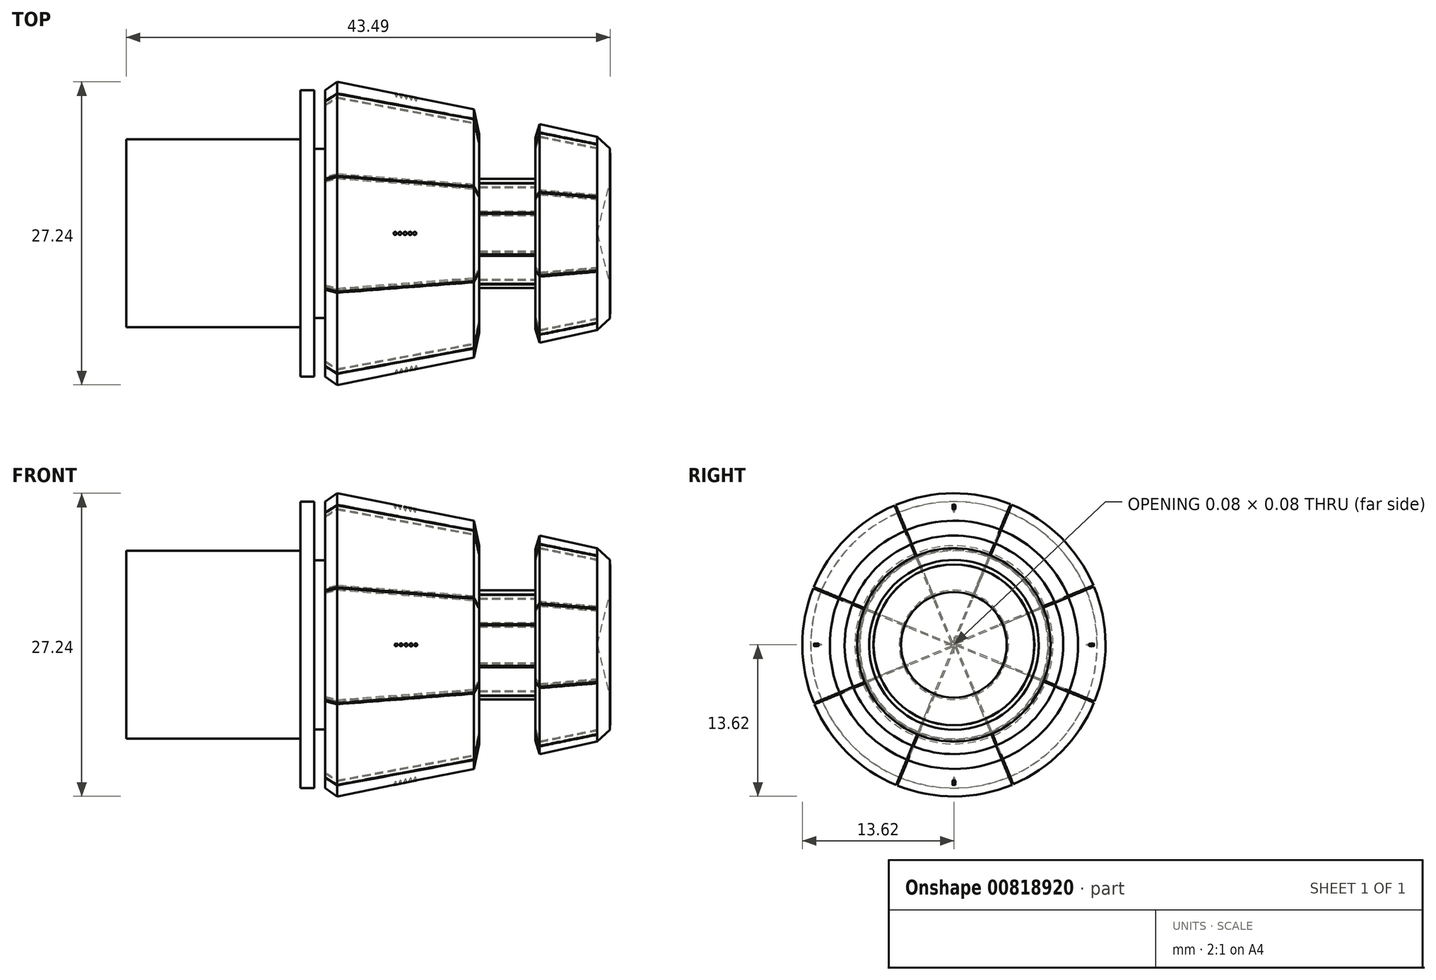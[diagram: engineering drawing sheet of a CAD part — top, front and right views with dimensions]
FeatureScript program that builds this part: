
annotation { "Feature Type Name" : "Feature", "Feature Type Description" : "" }
export const myFeature = defineFeature(function(context is Context, id is Id, definition is map)
    precondition{}
    {
        {
            var Q0;
            Q0=qCreatedBy(makeId("Front.planeOp"),FACE);
            var sketch = newSketch(context, id + "F0", { "sketchPlane" : qUnion([Q0])});
            skLineSegment(sketch, "E0", {"start": v(4.43, 0) * mm, "end": v(4.43, 12.88) * mm});
            skLineSegment(sketch, "E1", {"start": v(4.43, 12.88) * mm, "end": v(5.5, 13.62) * mm});
            skLineSegment(sketch, "E2", {"start": v(5.5, 13.62) * mm, "end": v(5.5, 0) * mm});
            skLineSegment(sketch, "E3", {"start": v(5.5, 0) * mm, "end": v(4.43, 0) * mm});
            skLineSegment(sketch, "E4", {"start": v(5.5, 13.62) * mm, "end": v(17.79, 11.15) * mm});
            skLineSegment(sketch, "E5", {"start": v(17.79, 11.15) * mm, "end": v(17.79, 0) * mm});
            skLineSegment(sketch, "E6", {"start": v(17.79, 0) * mm, "end": v(5.5, 0) * mm});
            skLineSegment(sketch, "E7", {"start": v(17.79, 11.15) * mm, "end": v(18.26, 8.9) * mm});
            skLineSegment(sketch, "E8", {"start": v(18.26, 8.9) * mm, "end": v(18.26, 0) * mm});
            skLineSegment(sketch, "E9", {"start": v(18.26, 0) * mm, "end": v(17.79, 0) * mm});
            skLineSegment(sketch, "E10", {"start": v(23.33, 8.59) * mm, "end": v(23.33, 0) * mm});
            skLineSegment(sketch, "E11", {"start": v(23.33, 0) * mm, "end": v(18.26, 0) * mm});
            skLineSegment(sketch, "E12", {"start": v(4.43, 0) * mm, "end": v(3.45, 0) * mm});
            skLineSegment(sketch, "E13", {"start": v(3.45, 0) * mm, "end": v(3.45, 7.6) * mm});
            skLineSegment(sketch, "E14", {"start": v(3.45, 7.6) * mm, "end": v(4.43, 7.6) * mm});
            skLineSegment(sketch, "E15", {"start": v(4.43, 7.6) * mm, "end": v(4.43, 0) * mm});
            skLineSegment(sketch, "E16", {"start": v(3.45, 0) * mm, "end": v(2.2, 0) * mm});
            skLineSegment(sketch, "E17", {"start": v(2.2, 0) * mm, "end": v(2.2, 12.87) * mm});
            skLineSegment(sketch, "E18", {"start": v(2.2, 12.87) * mm, "end": v(3.45, 12.87) * mm});
            skLineSegment(sketch, "E19", {"start": v(3.45, 12.87) * mm, "end": v(3.45, 7.6) * mm});
            skLineSegment(sketch, "E20", {"start": v(23.33, 8.59) * mm, "end": v(23.72, 9.82) * mm});
            skPoint(sketch, "E21.startSnap0", {"position": v(3.94, 7.6) * mm});
            skLineSegment(sketch, "E22", {"start": v(2.2, 8.45) * mm, "end": v(2.2, 0) * mm});
            skLineSegment(sketch, "E23", {"start": v(-13.45, 8.45) * mm, "end": v(-13.45, 0) * mm});
            skLineSegment(sketch, "E24", {"start": v(-13.45, 8.45) * mm, "end": v(2.2, 8.45) * mm});
            skLineSegment(sketch, "E25", {"start": v(-13.45, 0) * mm, "end": v(2.2, 0) * mm});
            skPoint(sketch, "E26", {"position": v(28.88, 8.7) * mm});
            skLineSegment(sketch, "E27", {"start": v(28.88, 8.7) * mm, "end": v(28.88, 0) * mm});
            skLineSegment(sketch, "E28", {"start": v(30.03, 7.63) * mm, "end": v(28.88, 8.7) * mm});
            skLineSegment(sketch, "E29", {"start": v(23.72, 9.82) * mm, "end": v(28.88, 8.7) * mm});
            skLineSegment(sketch, "E30", {"start": v(23.72, 9.82) * mm, "end": v(23.72, 0) * mm});
            skLineSegment(sketch, "E31", {"start": v(23.72, 0) * mm, "end": v(23.33, 0) * mm});
            skLineSegment(sketch, "E32", {"start": v(18.26, 0) * mm, "end": v(23.33, 0) * mm});
            skLineSegment(sketch, "E33", {"start": v(23.33, 4.91) * mm, "end": v(18.26, 4.91) * mm});
            skLineSegment(sketch, "E34", {"start": v(18.26, 4.91) * mm, "end": v(18.26, 0) * mm});
            skLineSegment(sketch, "E35", {"start": v(28.88, 0) * mm, "end": v(28.88, 8.7) * mm});
            skLineSegment(sketch, "E36", {"start": v(30.03, 7.63) * mm, "end": v(30.03, 4.75) * mm});
            skLineSegment(sketch, "E37", {"start": v(30.03, 4.75) * mm, "end": v(28.88, 0) * mm});
            skLineSegment(sketch, "E38", {"start": v(23.72, 0) * mm, "end": v(28.88, 0) * mm});
            skSolve(sketch);
        }
        {
            var Q0;
            Q0=qSketchRegion(id+"F0",true);
            var Q1;
            Q1=sQuery(id+"F0.wireOp",EDGE,"E12");
            revolve(context, id + "F1", {"surfaceOperationType" : NewSurfaceOperationType.NEW, "entities" : qUnion([Q0]), "axis" : qUnion([Q1]), "revolveType" : RevolveType.FULL});
        }
        {
            var Q0;
            Q0=qCreatedBy(makeId("Right.planeOp"),FACE);
            var sketch = newSketch(context, id + "F2", { "sketchPlane" : qUnion([Q0])});
            skLineSegment(sketch, "E39.bottom", {"start": v(-0.13, 0.07) * mm, "end": v(0, 0.02) * mm});
            skLineSegment(sketch, "E39.top", {"start": v(7.3, 17.98) * mm, "end": v(7.41, 17.93) * mm});
            skLineSegment(sketch, "E39.left", {"start": v(0, 0.02) * mm, "end": v(7.41, 17.93) * mm});
            skLineSegment(sketch, "E39.right", {"start": v(-0.13, 0.07) * mm, "end": v(7.3, 17.98) * mm});
            skLineSegment(sketch, "E40.1.0", {"start": v(-0.14, -0.04) * mm, "end": v(-7.56, 17.87) * mm});
            skLineSegment(sketch, "E40.1.1", {"start": v(-0.02, 0) * mm, "end": v(-7.44, 17.92) * mm});
            skLineSegment(sketch, "E40.1.2", {"start": v(-0.14, -0.04) * mm, "end": v(-0.02, 0) * mm});
            skLineSegment(sketch, "E40.1.3", {"start": v(-7.56, 17.87) * mm, "end": v(-7.44, 17.92) * mm});
            skLineSegment(sketch, "E40.2.0", {"start": v(-0.07, -0.13) * mm, "end": v(-17.98, 7.3) * mm});
            skLineSegment(sketch, "E40.2.1", {"start": v(-0.02, 0) * mm, "end": v(-17.93, 7.41) * mm});
            skLineSegment(sketch, "E40.2.2", {"start": v(-0.07, -0.13) * mm, "end": v(-0.02, 0) * mm});
            skLineSegment(sketch, "E40.2.3", {"start": v(-17.98, 7.3) * mm, "end": v(-17.93, 7.41) * mm});
            skLineSegment(sketch, "E40.3.0", {"start": v(0.04, -0.14) * mm, "end": v(-17.87, -7.56) * mm});
            skLineSegment(sketch, "E40.3.1", {"start": v(0, -0.02) * mm, "end": v(-17.92, -7.44) * mm});
            skLineSegment(sketch, "E40.3.2", {"start": v(0.04, -0.14) * mm, "end": v(0, -0.02) * mm});
            skLineSegment(sketch, "E40.3.3", {"start": v(-17.87, -7.56) * mm, "end": v(-17.92, -7.44) * mm});
            skLineSegment(sketch, "E40.4.0", {"start": v(0.13, -0.07) * mm, "end": v(-7.3, -17.98) * mm});
            skLineSegment(sketch, "E40.4.1", {"start": v(0, -0.02) * mm, "end": v(-7.41, -17.93) * mm});
            skLineSegment(sketch, "E40.4.2", {"start": v(0.13, -0.07) * mm, "end": v(0, -0.02) * mm});
            skLineSegment(sketch, "E40.4.3", {"start": v(-7.3, -17.98) * mm, "end": v(-7.41, -17.93) * mm});
            skLineSegment(sketch, "E40.5.0", {"start": v(0.14, 0.04) * mm, "end": v(7.56, -17.87) * mm});
            skLineSegment(sketch, "E40.5.1", {"start": v(0.02, 0) * mm, "end": v(7.44, -17.92) * mm});
            skLineSegment(sketch, "E40.5.2", {"start": v(0.14, 0.04) * mm, "end": v(0.02, 0) * mm});
            skLineSegment(sketch, "E40.5.3", {"start": v(7.56, -17.87) * mm, "end": v(7.44, -17.92) * mm});
            skLineSegment(sketch, "E40.6.0", {"start": v(0.07, 0.13) * mm, "end": v(17.98, -7.3) * mm});
            skLineSegment(sketch, "E40.6.1", {"start": v(0.02, 0) * mm, "end": v(17.93, -7.41) * mm});
            skLineSegment(sketch, "E40.6.2", {"start": v(0.07, 0.13) * mm, "end": v(0.02, 0) * mm});
            skLineSegment(sketch, "E40.6.3", {"start": v(17.98, -7.3) * mm, "end": v(17.93, -7.41) * mm});
            skLineSegment(sketch, "E40.7.0", {"start": v(-0.04, 0.14) * mm, "end": v(17.87, 7.56) * mm});
            skLineSegment(sketch, "E40.7.1", {"start": v(0, 0.02) * mm, "end": v(17.92, 7.44) * mm});
            skLineSegment(sketch, "E40.7.2", {"start": v(-0.04, 0.14) * mm, "end": v(0, 0.02) * mm});
            skLineSegment(sketch, "E40.7.3", {"start": v(17.87, 7.56) * mm, "end": v(17.92, 7.44) * mm});
            skPoint(sketch, "E40.center", {"position": v(0, 0) * mm});
            skSolve(sketch);
        }
        {
            var Q0;
            Q0 = qSketchRegion(id + "F2", true);
            var Q1;
            Q1=makeQuery(id+"F1.opRevolve","SWEPT_VERTEX",VERTEX,{"disambiguationData":[OSD([sQuery(id+"F0.wireOp",EDGE,"E35"),sQuery(id+"F0.wireOp",EDGE,"E37"),sQuery(id+"F0.wireOp",EDGE,"E38")])]});
            var Q2;
            Q2=makeQuery(id+"F1.opRevolve","SWEPT_FACE",FACE,{"disambiguationData":[OSD([sQuery(id+"F0.wireOp",EDGE,"E0")])]});
            extrude(context, id + "F3", {"entities" : qUnion([Q0]), "operationType" : NewBodyOperationType.REMOVE, "endBound" : BoundingType.UP_TO_VERTEX, "depth" : 37.08 * mm, "endBoundEntityVertex" : qUnion([Q1]), "offsetDistance" : 25.4 * mm, "hasSecondDirection" : true, "secondDirectionBound" : SecondDirectionBoundingType.UP_TO_SURFACE, "secondDirectionOppositeDirection" : false, "secondDirectionDepth" : 4.32 * mm, "secondDirectionBoundEntityFace" : qUnion([Q2])});
        }
        {
            var Q0;
            Q0=qCreatedBy(makeId("Front.planeOp"),FACE);
            var sketch = newSketch(context, id + "F4", { "sketchPlane" : qUnion([Q0])});
            skLineSegment(sketch, "E41", {"start": v(4.44, 0) * mm, "end": v(4.44, 12.88) * mm});
            skLineSegment(sketch, "E42", {"start": v(4.44, 12.48) * mm, "end": v(5.52, 13.22) * mm});
            skLineSegment(sketch, "E43", {"start": v(5.52, 13.62) * mm, "end": v(5.52, 0) * mm});
            skLineSegment(sketch, "E44", {"start": v(5.52, 0) * mm, "end": v(4.44, 0) * mm});
            skLineSegment(sketch, "E45", {"start": v(5.52, 13.22) * mm, "end": v(17.8, 10.75) * mm});
            skLineSegment(sketch, "E46", {"start": v(17.8, 11.15) * mm, "end": v(17.8, 0) * mm});
            skLineSegment(sketch, "E47", {"start": v(17.8, 0) * mm, "end": v(5.52, 0) * mm});
            skLineSegment(sketch, "E48", {"start": v(17.8, 10.75) * mm, "end": v(18.27, 8.5) * mm});
            skLineSegment(sketch, "E49", {"start": v(18.27, 8.9) * mm, "end": v(18.27, 0) * mm});
            skLineSegment(sketch, "E50", {"start": v(18.27, 0) * mm, "end": v(17.8, 0) * mm});
            skLineSegment(sketch, "E51", {"start": v(23.34, 8.59) * mm, "end": v(23.34, 0) * mm});
            skLineSegment(sketch, "E52", {"start": v(23.34, 0) * mm, "end": v(18.27, 0) * mm});
            skLineSegment(sketch, "E53", {"start": v(4.44, 7.6) * mm, "end": v(4.44, 0) * mm});
            skLineSegment(sketch, "E54", {"start": v(23.34, 8.18) * mm, "end": v(23.72, 9.42) * mm});
            skLineSegment(sketch, "E55", {"start": v(2.2, 8.45) * mm, "end": v(2.2, 0) * mm});
            skPoint(sketch, "E56", {"position": v(28.89, 8.29) * mm});
            skLineSegment(sketch, "E57", {"start": v(28.89, 8.7) * mm, "end": v(28.89, 0) * mm});
            skLineSegment(sketch, "E58", {"start": v(30.04, 7.22) * mm, "end": v(28.89, 8.29) * mm});
            skLineSegment(sketch, "E59", {"start": v(23.72, 9.42) * mm, "end": v(28.89, 8.29) * mm});
            skLineSegment(sketch, "E60", {"start": v(23.72, 9.82) * mm, "end": v(23.72, 0) * mm});
            skLineSegment(sketch, "E61", {"start": v(23.72, 0) * mm, "end": v(23.34, 0) * mm});
            skLineSegment(sketch, "E62", {"start": v(18.27, 0) * mm, "end": v(23.34, 0) * mm});
            skLineSegment(sketch, "E63", {"start": v(23.34, 4.5) * mm, "end": v(18.27, 4.5) * mm});
            skLineSegment(sketch, "E64", {"start": v(18.27, 4.91) * mm, "end": v(18.27, 0) * mm});
            skLineSegment(sketch, "E65", {"start": v(28.89, 0) * mm, "end": v(28.89, 8.7) * mm});
            skLineSegment(sketch, "E66", {"start": v(30.04, 7.63) * mm, "end": v(30.04, 4.75) * mm});
            skLineSegment(sketch, "E67", {"start": v(30.04, 4.75) * mm, "end": v(28.89, 0) * mm});
            skLineSegment(sketch, "E68", {"start": v(23.72, 0) * mm, "end": v(28.89, 0) * mm});
            skSolve(sketch);
        }
        {
            var Q0;
            Q0 = qSketchRegion(id + "F4", true);
            var Q1;
            Q1=sQuery(id+"F4.wireOp",EDGE,"E47");
            revolve(context, id + "F5", {"operationType" : NewBodyOperationType.ADD, "surfaceOperationType" : NewSurfaceOperationType.NEW, "entities" : qUnion([Q0]), "axis" : qUnion([Q1]), "revolveType" : RevolveType.FULL});
        }
        {
            var Q0;
            Q0=qCreatedBy(makeId("Top.planeOp"),FACE);
            var sketch = newSketch(context, id + "F6", { "sketchPlane" : qUnion([Q0])});
            skLineSegment(sketch, "E69.MirrorCS", {"start": v(11.9, -12.5) * mm, "end": v(11.74, -12.03) * mm});
            skLineSegment(sketch, "E70.MirrorCS", {"start": v(11.71, -12.5) * mm, "end": v(11.9, -12.5) * mm});
            skLineSegment(sketch, "E71.MirrorCS", {"start": v(11.74, -12.03) * mm, "end": v(11.71, -12.5) * mm});
            skLineSegment(sketch, "E72.MirrorCS", {"start": v(12.35, -12.42) * mm, "end": v(12.2, -11.94) * mm});
            skLineSegment(sketch, "E73.MirrorCS", {"start": v(12.16, -12.4) * mm, "end": v(12.35, -12.42) * mm});
            skLineSegment(sketch, "E74.MirrorCS", {"start": v(12.2, -11.94) * mm, "end": v(12.16, -12.4) * mm});
            skLineSegment(sketch, "E75.MirrorCS", {"start": v(11.44, -12.62) * mm, "end": v(11.28, -12.14) * mm});
            skLineSegment(sketch, "E76.MirrorCS", {"start": v(11.25, -12.6) * mm, "end": v(11.44, -12.62) * mm});
            skLineSegment(sketch, "E77.MirrorCS", {"start": v(11.28, -12.14) * mm, "end": v(11.25, -12.6) * mm});
            skLineSegment(sketch, "E78.MirrorCS", {"start": v(11, -12.71) * mm, "end": v(10.85, -12.24) * mm});
            skLineSegment(sketch, "E79.MirrorCS", {"start": v(10.81, -12.7) * mm, "end": v(11, -12.71) * mm});
            skLineSegment(sketch, "E80.MirrorCS", {"start": v(10.85, -12.24) * mm, "end": v(10.81, -12.7) * mm});
            skLineSegment(sketch, "E81.MirrorCS", {"start": v(12.76, -12.35) * mm, "end": v(12.61, -11.88) * mm});
            skLineSegment(sketch, "E82.MirrorCS", {"start": v(12.58, -12.34) * mm, "end": v(12.76, -12.35) * mm});
            skLineSegment(sketch, "E83.MirrorCS", {"start": v(12.61, -11.88) * mm, "end": v(12.58, -12.34) * mm});
            skLineSegment(sketch, "E84.MirrorCS", {"start": v(11.28, 12.14) * mm, "end": v(11.25, 12.6) * mm});
            skLineSegment(sketch, "E85.MirrorCS", {"start": v(11.71, 12.5) * mm, "end": v(11.9, 12.5) * mm});
            skLineSegment(sketch, "E86.MirrorCS", {"start": v(11.25, 12.6) * mm, "end": v(11.44, 12.62) * mm});
            skLineSegment(sketch, "E87.MirrorCS", {"start": v(12.35, 12.42) * mm, "end": v(12.2, 11.94) * mm});
            skLineSegment(sketch, "E88.MirrorCS", {"start": v(11, 12.71) * mm, "end": v(10.85, 12.24) * mm});
            skLineSegment(sketch, "E89.MirrorCS", {"start": v(10.81, 12.7) * mm, "end": v(11, 12.71) * mm});
            skLineSegment(sketch, "E90.MirrorCS", {"start": v(11.74, 12.03) * mm, "end": v(11.71, 12.5) * mm});
            skLineSegment(sketch, "E91.MirrorCS", {"start": v(12.58, 12.34) * mm, "end": v(12.76, 12.35) * mm});
            skLineSegment(sketch, "E92.MirrorCS", {"start": v(11.44, 12.62) * mm, "end": v(11.28, 12.14) * mm});
            skLineSegment(sketch, "E93.MirrorCS", {"start": v(12.76, 12.35) * mm, "end": v(12.61, 11.88) * mm});
            skLineSegment(sketch, "E94.MirrorCS", {"start": v(10.85, 12.24) * mm, "end": v(10.81, 12.7) * mm});
            skLineSegment(sketch, "E95.MirrorCS", {"start": v(12.61, 11.88) * mm, "end": v(12.58, 12.34) * mm});
            skLineSegment(sketch, "E96.MirrorCS", {"start": v(12.16, 12.4) * mm, "end": v(12.35, 12.42) * mm});
            skLineSegment(sketch, "E97.MirrorCS", {"start": v(11.9, 12.5) * mm, "end": v(11.74, 12.03) * mm});
            skLineSegment(sketch, "E98.MirrorCS", {"start": v(12.2, 11.94) * mm, "end": v(12.16, 12.4) * mm});
            skSolve(sketch);
        }
        {
            var Q0;
            Q0=makeQuery(id+"F6.imprint","IMPRINT",FACE,{"disambiguationData":[TD([[makeQuery(id+"F6.imprint","IMPRINT",EDGE,{"derivedFrom":sQuery(id+"F6.wireOp",EDGE,"E78.MirrorCS")}),1.0]])]});
            var Q1;
            Q1=sQuery(id+"F6.wireOp",EDGE,"E80.MirrorCS");
            revolve(context, id + "F7", {"operationType" : NewBodyOperationType.REMOVE, "surfaceOperationType" : NewSurfaceOperationType.NEW, "entities" : qUnion([Q0]), "axis" : qUnion([Q1]), "revolveType" : RevolveType.FULL, "oppositeDirection" : true});
        }
        {
            var Q0;
            Q0=makeQuery(id+"F6.imprint","IMPRINT",FACE,{"disambiguationData":[TD([[makeQuery(id+"F6.imprint","IMPRINT",EDGE,{"derivedFrom":sQuery(id+"F6.wireOp",EDGE,"E75.MirrorCS")}),1.0]])]});
            var Q1;
            Q1=sQuery(id+"F6.wireOp",EDGE,"E77.MirrorCS");
            revolve(context, id + "F8", {"operationType" : NewBodyOperationType.REMOVE, "surfaceOperationType" : NewSurfaceOperationType.NEW, "entities" : qUnion([Q0]), "axis" : qUnion([Q1]), "revolveType" : RevolveType.FULL, "oppositeDirection" : true});
        }
        {
            var Q0;
            Q0=makeQuery(id+"F6.imprint","IMPRINT",FACE,{"disambiguationData":[TD([[makeQuery(id+"F6.imprint","IMPRINT",EDGE,{"derivedFrom":sQuery(id+"F6.wireOp",EDGE,"E69.MirrorCS")}),1.0]])]});
            var Q1;
            Q1=sQuery(id+"F6.wireOp",EDGE,"E71.MirrorCS");
            revolve(context, id + "F9", {"operationType" : NewBodyOperationType.REMOVE, "surfaceOperationType" : NewSurfaceOperationType.NEW, "entities" : qUnion([Q0]), "axis" : qUnion([Q1]), "revolveType" : RevolveType.FULL, "oppositeDirection" : true});
        }
        {
            var Q0;
            Q0=makeQuery(id+"F6.imprint","IMPRINT",FACE,{"disambiguationData":[TD([[makeQuery(id+"F6.imprint","IMPRINT",EDGE,{"derivedFrom":sQuery(id+"F6.wireOp",EDGE,"E72.MirrorCS")}),1.0]])]});
            var Q1;
            Q1=sQuery(id+"F6.wireOp",EDGE,"E74.MirrorCS");
            revolve(context, id + "F10", {"operationType" : NewBodyOperationType.REMOVE, "surfaceOperationType" : NewSurfaceOperationType.NEW, "entities" : qUnion([Q0]), "axis" : qUnion([Q1]), "revolveType" : RevolveType.FULL, "oppositeDirection" : true});
        }
        {
            var Q0;
            Q0=makeQuery(id+"F6.imprint","IMPRINT",FACE,{"disambiguationData":[TD([[makeQuery(id+"F6.imprint","IMPRINT",EDGE,{"derivedFrom":sQuery(id+"F6.wireOp",EDGE,"E81.MirrorCS")}),1.0]])]});
            var Q1;
            Q1=sQuery(id+"F6.wireOp",EDGE,"E83.MirrorCS");
            revolve(context, id + "F11", {"operationType" : NewBodyOperationType.REMOVE, "surfaceOperationType" : NewSurfaceOperationType.NEW, "entities" : qUnion([Q0]), "axis" : qUnion([Q1]), "revolveType" : RevolveType.FULL, "oppositeDirection" : true});
        }
        {
            var Q0;
            Q0=makeQuery(id+"F6.imprint","IMPRINT",FACE,{"disambiguationData":[TD([[makeQuery(id+"F6.imprint","IMPRINT",EDGE,{"derivedFrom":sQuery(id+"F6.wireOp",EDGE,"E88.MirrorCS")}),-1.0]])]});
            var Q1;
            Q1=sQuery(id+"F6.wireOp",EDGE,"E94.MirrorCS");
            revolve(context, id + "F12", {"operationType" : NewBodyOperationType.REMOVE, "surfaceOperationType" : NewSurfaceOperationType.NEW, "entities" : qUnion([Q0]), "axis" : qUnion([Q1]), "revolveType" : RevolveType.FULL, "oppositeDirection" : true});
        }
        {
            var Q0;
            Q0=makeQuery(id+"F6.imprint","IMPRINT",FACE,{"disambiguationData":[TD([[makeQuery(id+"F6.imprint","IMPRINT",EDGE,{"derivedFrom":sQuery(id+"F6.wireOp",EDGE,"E84.MirrorCS")}),-1.0]])]});
            var Q1;
            Q1=sQuery(id+"F6.wireOp",EDGE,"E84.MirrorCS");
            revolve(context, id + "F13", {"operationType" : NewBodyOperationType.REMOVE, "surfaceOperationType" : NewSurfaceOperationType.NEW, "entities" : qUnion([Q0]), "axis" : qUnion([Q1]), "revolveType" : RevolveType.FULL, "oppositeDirection" : true});
        }
        {
            var Q0;
            Q0=makeQuery(id+"F6.imprint","IMPRINT",FACE,{"disambiguationData":[TD([[makeQuery(id+"F6.imprint","IMPRINT",EDGE,{"derivedFrom":sQuery(id+"F6.wireOp",EDGE,"E85.MirrorCS")}),-1.0]])]});
            var Q1;
            Q1=sQuery(id+"F6.wireOp",EDGE,"E90.MirrorCS");
            revolve(context, id + "F14", {"operationType" : NewBodyOperationType.REMOVE, "surfaceOperationType" : NewSurfaceOperationType.NEW, "entities" : qUnion([Q0]), "axis" : qUnion([Q1]), "revolveType" : RevolveType.FULL, "oppositeDirection" : true});
        }
        {
            var Q0;
            Q0=makeQuery(id+"F6.imprint","IMPRINT",FACE,{"disambiguationData":[TD([[makeQuery(id+"F6.imprint","IMPRINT",EDGE,{"derivedFrom":sQuery(id+"F6.wireOp",EDGE,"E87.MirrorCS")}),-1.0]])]});
            var Q1;
            Q1=sQuery(id+"F6.wireOp",EDGE,"E98.MirrorCS");
            revolve(context, id + "F15", {"operationType" : NewBodyOperationType.REMOVE, "surfaceOperationType" : NewSurfaceOperationType.NEW, "entities" : qUnion([Q0]), "axis" : qUnion([Q1]), "revolveType" : RevolveType.FULL, "oppositeDirection" : true});
        }
        {
            var Q0;
            Q0=makeQuery(id+"F6.imprint","IMPRINT",FACE,{"disambiguationData":[TD([[makeQuery(id+"F6.imprint","IMPRINT",EDGE,{"derivedFrom":sQuery(id+"F6.wireOp",EDGE,"E91.MirrorCS")}),-1.0]])]});
            var Q1;
            Q1=sQuery(id+"F6.wireOp",EDGE,"E95.MirrorCS");
            revolve(context, id + "F16", {"operationType" : NewBodyOperationType.REMOVE, "surfaceOperationType" : NewSurfaceOperationType.NEW, "entities" : qUnion([Q0]), "axis" : qUnion([Q1]), "revolveType" : RevolveType.FULL, "oppositeDirection" : true});
        }
        {
            var Q0;
            Q0=qCreatedBy(makeId("Front.planeOp"),FACE);
            var sketch = newSketch(context, id + "F17", { "sketchPlane" : qUnion([Q0])});
            skLineSegment(sketch, "E99.MirrorCS", {"start": v(11.8, -12.5) * mm, "end": v(11.65, -12.03) * mm});
            skLineSegment(sketch, "E100.MirrorCS", {"start": v(11.62, -12.5) * mm, "end": v(11.8, -12.5) * mm});
            skLineSegment(sketch, "E101.MirrorCS", {"start": v(11.65, -12.03) * mm, "end": v(11.62, -12.5) * mm});
            skLineSegment(sketch, "E102.MirrorCS", {"start": v(12.25, -12.42) * mm, "end": v(12.1, -11.94) * mm});
            skLineSegment(sketch, "E103.MirrorCS", {"start": v(12.07, -12.4) * mm, "end": v(12.25, -12.42) * mm});
            skLineSegment(sketch, "E104.MirrorCS", {"start": v(12.1, -11.94) * mm, "end": v(12.07, -12.4) * mm});
            skLineSegment(sketch, "E105.MirrorCS", {"start": v(11.34, -12.62) * mm, "end": v(11.2, -12.14) * mm});
            skLineSegment(sketch, "E106.MirrorCS", {"start": v(11.16, -12.6) * mm, "end": v(11.34, -12.62) * mm});
            skLineSegment(sketch, "E107.MirrorCS", {"start": v(11.2, -12.14) * mm, "end": v(11.16, -12.6) * mm});
            skLineSegment(sketch, "E108.MirrorCS", {"start": v(10.9, -12.71) * mm, "end": v(10.75, -12.24) * mm});
            skLineSegment(sketch, "E109.MirrorCS", {"start": v(10.72, -12.7) * mm, "end": v(10.9, -12.71) * mm});
            skLineSegment(sketch, "E110.MirrorCS", {"start": v(10.75, -12.24) * mm, "end": v(10.72, -12.7) * mm});
            skLineSegment(sketch, "E111.MirrorCS", {"start": v(12.67, -12.35) * mm, "end": v(12.52, -11.88) * mm});
            skLineSegment(sketch, "E112.MirrorCS", {"start": v(12.49, -12.34) * mm, "end": v(12.67, -12.35) * mm});
            skLineSegment(sketch, "E113.MirrorCS", {"start": v(12.52, -11.88) * mm, "end": v(12.49, -12.34) * mm});
            skLineSegment(sketch, "E114.MirrorCS", {"start": v(11.2, 12.14) * mm, "end": v(11.16, 12.6) * mm});
            skLineSegment(sketch, "E115.MirrorCS", {"start": v(11.62, 12.5) * mm, "end": v(11.8, 12.5) * mm});
            skLineSegment(sketch, "E116.MirrorCS", {"start": v(11.16, 12.6) * mm, "end": v(11.34, 12.62) * mm});
            skLineSegment(sketch, "E117.MirrorCS", {"start": v(12.25, 12.42) * mm, "end": v(12.1, 11.94) * mm});
            skLineSegment(sketch, "E118.MirrorCS", {"start": v(10.9, 12.71) * mm, "end": v(10.75, 12.24) * mm});
            skLineSegment(sketch, "E119.MirrorCS", {"start": v(10.72, 12.7) * mm, "end": v(10.9, 12.71) * mm});
            skLineSegment(sketch, "E120.MirrorCS", {"start": v(11.65, 12.03) * mm, "end": v(11.62, 12.5) * mm});
            skLineSegment(sketch, "E121.MirrorCS", {"start": v(12.49, 12.34) * mm, "end": v(12.67, 12.35) * mm});
            skLineSegment(sketch, "E122.MirrorCS", {"start": v(11.34, 12.62) * mm, "end": v(11.2, 12.14) * mm});
            skLineSegment(sketch, "E123.MirrorCS", {"start": v(12.67, 12.35) * mm, "end": v(12.52, 11.88) * mm});
            skLineSegment(sketch, "E124.MirrorCS", {"start": v(10.75, 12.24) * mm, "end": v(10.72, 12.7) * mm});
            skLineSegment(sketch, "E125.MirrorCS", {"start": v(12.52, 11.88) * mm, "end": v(12.49, 12.34) * mm});
            skLineSegment(sketch, "E126.MirrorCS", {"start": v(12.07, 12.4) * mm, "end": v(12.25, 12.42) * mm});
            skLineSegment(sketch, "E127.MirrorCS", {"start": v(11.8, 12.5) * mm, "end": v(11.65, 12.03) * mm});
            skLineSegment(sketch, "E128.MirrorCS", {"start": v(12.1, 11.94) * mm, "end": v(12.07, 12.4) * mm});
            skSolve(sketch);
        }
        {
            var Q0;
            Q0=makeQuery(id+"F17.imprint","IMPRINT",FACE,{"disambiguationData":[TD([[makeQuery(id+"F17.imprint","IMPRINT",EDGE,{"derivedFrom":sQuery(id+"F17.wireOp",EDGE,"E99.MirrorCS")}),1.0]])]});
            var Q1;
            Q1=sQuery(id+"F17.wireOp",EDGE,"E101.MirrorCS");
            revolve(context, id + "F18", {"operationType" : NewBodyOperationType.REMOVE, "surfaceOperationType" : NewSurfaceOperationType.NEW, "entities" : qUnion([Q0]), "axis" : qUnion([Q1]), "revolveType" : RevolveType.FULL, "oppositeDirection" : true});
        }
        {
            var Q0;
            Q0=makeQuery(id+"F17.imprint","IMPRINT",FACE,{"disambiguationData":[TD([[makeQuery(id+"F17.imprint","IMPRINT",EDGE,{"derivedFrom":sQuery(id+"F17.wireOp",EDGE,"E108.MirrorCS")}),1.0]])]});
            var Q1;
            Q1=sQuery(id+"F17.wireOp",EDGE,"E110.MirrorCS");
            revolve(context, id + "F19", {"operationType" : NewBodyOperationType.REMOVE, "surfaceOperationType" : NewSurfaceOperationType.NEW, "entities" : qUnion([Q0]), "axis" : qUnion([Q1]), "revolveType" : RevolveType.FULL, "oppositeDirection" : true});
        }
        {
            var Q0;
            Q0=makeQuery(id+"F17.imprint","IMPRINT",FACE,{"disambiguationData":[TD([[makeQuery(id+"F17.imprint","IMPRINT",EDGE,{"derivedFrom":sQuery(id+"F17.wireOp",EDGE,"E105.MirrorCS")}),1.0]])]});
            var Q1;
            Q1=sQuery(id+"F17.wireOp",EDGE,"E107.MirrorCS");
            revolve(context, id + "F20", {"operationType" : NewBodyOperationType.REMOVE, "surfaceOperationType" : NewSurfaceOperationType.NEW, "entities" : qUnion([Q0]), "axis" : qUnion([Q1]), "revolveType" : RevolveType.FULL});
        }
        {
            var Q0;
            Q0=makeQuery(id+"F17.imprint","IMPRINT",FACE,{"disambiguationData":[TD([[makeQuery(id+"F17.imprint","IMPRINT",EDGE,{"derivedFrom":sQuery(id+"F17.wireOp",EDGE,"E102.MirrorCS")}),1.0]])]});
            var Q1;
            Q1=sQuery(id+"F17.wireOp",EDGE,"E104.MirrorCS");
            revolve(context, id + "F21", {"operationType" : NewBodyOperationType.REMOVE, "surfaceOperationType" : NewSurfaceOperationType.NEW, "entities" : qUnion([Q0]), "axis" : qUnion([Q1]), "revolveType" : RevolveType.FULL, "oppositeDirection" : true});
        }
        {
            var Q0;
            Q0=makeQuery(id+"F17.imprint","IMPRINT",FACE,{"disambiguationData":[TD([[makeQuery(id+"F17.imprint","IMPRINT",EDGE,{"derivedFrom":sQuery(id+"F17.wireOp",EDGE,"E111.MirrorCS")}),1.0]])]});
            var Q1;
            Q1=sQuery(id+"F17.wireOp",EDGE,"E113.MirrorCS");
            revolve(context, id + "F22", {"operationType" : NewBodyOperationType.REMOVE, "surfaceOperationType" : NewSurfaceOperationType.NEW, "entities" : qUnion([Q0]), "axis" : qUnion([Q1]), "revolveType" : RevolveType.FULL, "oppositeDirection" : true});
        }
        {
            var Q0;
            Q0=makeQuery(id+"F17.imprint","IMPRINT",FACE,{"disambiguationData":[TD([[makeQuery(id+"F17.imprint","IMPRINT",EDGE,{"derivedFrom":sQuery(id+"F17.wireOp",EDGE,"E118.MirrorCS")}),-1.0]])]});
            var Q1;
            Q1=sQuery(id+"F17.wireOp",EDGE,"E124.MirrorCS");
            revolve(context, id + "F23", {"operationType" : NewBodyOperationType.REMOVE, "surfaceOperationType" : NewSurfaceOperationType.NEW, "entities" : qUnion([Q0]), "axis" : qUnion([Q1]), "revolveType" : RevolveType.FULL, "oppositeDirection" : true});
        }
        {
            var Q0;
            Q0=makeQuery(id+"F17.imprint","IMPRINT",FACE,{"disambiguationData":[TD([[makeQuery(id+"F17.imprint","IMPRINT",EDGE,{"derivedFrom":sQuery(id+"F17.wireOp",EDGE,"E114.MirrorCS")}),-1.0]])]});
            var Q1;
            Q1=sQuery(id+"F17.wireOp",EDGE,"E114.MirrorCS");
            revolve(context, id + "F24", {"operationType" : NewBodyOperationType.REMOVE, "surfaceOperationType" : NewSurfaceOperationType.NEW, "entities" : qUnion([Q0]), "axis" : qUnion([Q1]), "revolveType" : RevolveType.FULL, "oppositeDirection" : true});
        }
        {
            var Q0;
            Q0=makeQuery(id+"F17.imprint","IMPRINT",FACE,{"disambiguationData":[TD([[makeQuery(id+"F17.imprint","IMPRINT",EDGE,{"derivedFrom":sQuery(id+"F17.wireOp",EDGE,"E115.MirrorCS")}),-1.0]])]});
            var Q1;
            Q1=sQuery(id+"F17.wireOp",EDGE,"E120.MirrorCS");
            revolve(context, id + "F25", {"operationType" : NewBodyOperationType.REMOVE, "surfaceOperationType" : NewSurfaceOperationType.NEW, "entities" : qUnion([Q0]), "axis" : qUnion([Q1]), "revolveType" : RevolveType.FULL, "oppositeDirection" : true});
        }
        {
            var Q0;
            Q0=makeQuery(id+"F17.imprint","IMPRINT",FACE,{"disambiguationData":[TD([[makeQuery(id+"F17.imprint","IMPRINT",EDGE,{"derivedFrom":sQuery(id+"F17.wireOp",EDGE,"E117.MirrorCS")}),-1.0]])]});
            var Q1;
            Q1=sQuery(id+"F17.wireOp",EDGE,"E128.MirrorCS");
            revolve(context, id + "F26", {"operationType" : NewBodyOperationType.REMOVE, "surfaceOperationType" : NewSurfaceOperationType.NEW, "entities" : qUnion([Q0]), "axis" : qUnion([Q1]), "revolveType" : RevolveType.FULL, "oppositeDirection" : true});
        }
        {
            var Q0;
            Q0=makeQuery(id+"F17.imprint","IMPRINT",FACE,{"disambiguationData":[TD([[makeQuery(id+"F17.imprint","IMPRINT",EDGE,{"derivedFrom":sQuery(id+"F17.wireOp",EDGE,"E121.MirrorCS")}),-1.0]])]});
            var Q1;
            Q1=sQuery(id+"F17.wireOp",EDGE,"E125.MirrorCS");
            revolve(context, id + "F27", {"operationType" : NewBodyOperationType.REMOVE, "surfaceOperationType" : NewSurfaceOperationType.NEW, "entities" : qUnion([Q0]), "axis" : qUnion([Q1]), "revolveType" : RevolveType.FULL, "oppositeDirection" : true});
        }
    });
